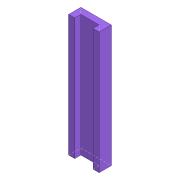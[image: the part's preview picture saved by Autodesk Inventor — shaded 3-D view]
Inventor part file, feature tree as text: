
AUTODESK INVENTOR PART (.ipt)
format: ipt  version: 2021 (Build 250183000, 183)  size: 85,504 bytes
history: native  units: mm
features: extrude x1, sketch x1
ambient origin geometry x8: Origin, YZ Plane, XZ Plane, XY Plane, X Axis, Y Axis, Z Axis, Center Point
bodies: Solid1 (feature_tree)
feature tree (2):
  extrude  "Extrusion1"  Depth=10.0mm
  sketch  "Sketch1"  dims[d0=30.0mm d1=10.0mm d2=10.0mm d3=10.0mm d4=10.0mm d5=200.0mm d6=0.0mm]
